# Revit family: ALE_RB80_C80
name_source: partatom
category: Equipement spécialisé
revit_build: Autodesk Revit 2017 (Build: 20160225_1515(x64)
units: mm (PartAtom-declared; Revit-internal decimal feet)

## family parameters
Basée sur le plan de construction = Non
Cote de connecteur circulaire = Utiliser le diamètre
Couper avec des vides une fois chargée = Non
Partagée = Non
Point de calcul de pièce = Non
Toujours verticalement = Oui
Type d'élément = Normal

## types (2) — shared parameters
Fabricant = AMCO Les Escamotables
Hauteur_barrière = 380 mm
URL = http://bornes-escamotables.com
epaisseur_cadre = 30 mm  [stored 0.0984252 ft]
hauteur_massif = 1200 mm
largeur = 1390 mm  [stored 4.56037 ft]
largeur_massif = 2500 mm
largeur_plaque = 1340 mm
matèriau_barrière = POSTE ESCAMOTABLE
matériau_cadre = PLAQUE AU SOL
matériau_massif = MASSIF BETON

## per-type parameters (varying)
| type | L1 | L2 | Modèle | epaisseur_plaque | longueur | longueur_massif |
| ALE RoadBlocker - 3030 mm x 1390 mm | 1515 mm  [stored 4.97047 ft] | 3030 mm  [stored 9.94094 ft] | RB80 C80 | 30 mm  [stored 0.0984252 ft] | 3030 mm  [stored 9.94094 ft] | 4000 mm  [stored 13.1234 ft] |
| ALE RoadBlocker - 3930 mm x 1390 mm | 1965 mm | 3930 mm  [stored 12.8937 ft] | RB35 C50 | 20 mm  [stored 0.0656168 ft] | 3930 mm  [stored 12.8937 ft] | 4900 mm  [stored 16.0761 ft] |

note: [stored X ft] marks values corroborated as IEEE doubles in the binary element streams (Revit-internal decimal feet)
